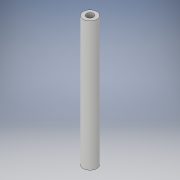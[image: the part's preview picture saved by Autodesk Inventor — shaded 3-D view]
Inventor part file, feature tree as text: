
AUTODESK INVENTOR PART (.ipt)
format: ipt  version: 2017 (Build 210142000, 142)  size: 93,184 bytes
history: native  units: in
note: dims shown in document units (in); Inventor stores cm internally (conversion verified against a paired STEP export)
features: extrude x1, sketch x1
ambient origin geometry x8: Origin, YZ Plane, XZ Plane, XY Plane, X Axis, Y Axis, Z Axis, Center Point
bodies: Solid1 (feature_tree)
feature tree (2):
  extrude  "Extrusion1"  Depth=2.375in
  sketch  "Sketch1"  dims[d0=0.125in d1=0.25in d2=2.375in d3=0.0in]
